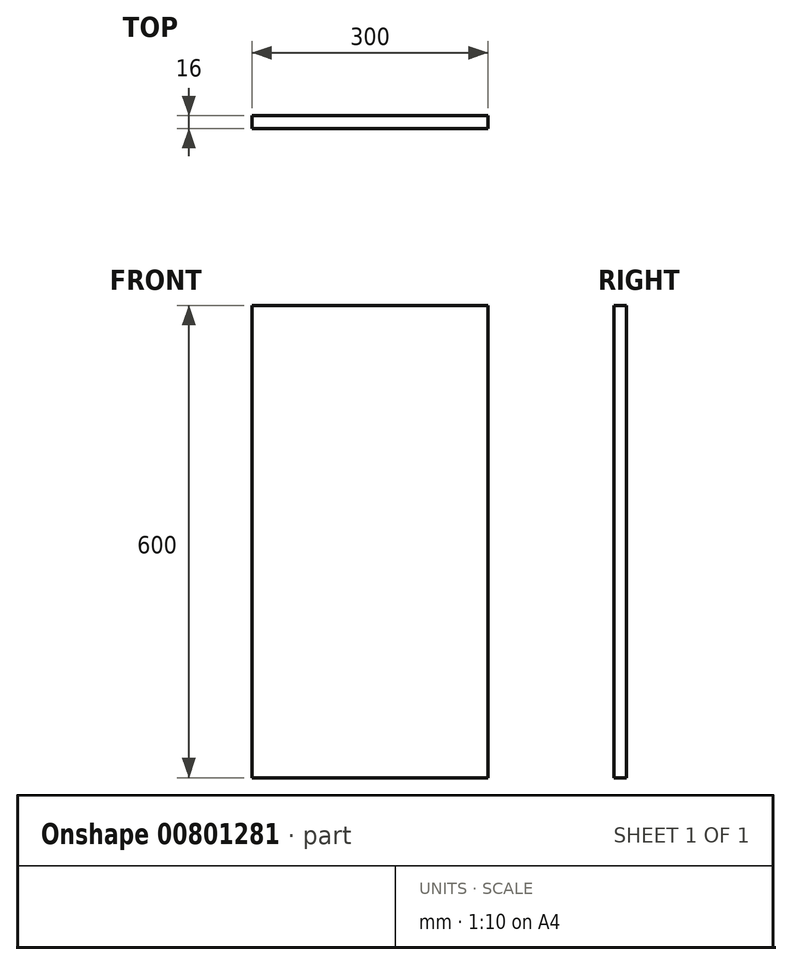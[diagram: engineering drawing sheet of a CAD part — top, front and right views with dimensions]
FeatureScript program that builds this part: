
annotation { "Feature Type Name" : "Feature", "Feature Type Description" : "" }
export const myFeature = defineFeature(function(context is Context, id is Id, definition is map)
    precondition{}
    {
        {
            var Q0;
            Q0=qCreatedBy(makeId("Front.planeOp"),FACE);
            var sketch = newSketch(context, id + "F0", { "sketchPlane" : qUnion([Q0])});
            skLineSegment(sketch, "E0.bottom", {"start": v(-150, -300) * mm, "end": v(150, -300) * mm});
            skLineSegment(sketch, "E0.top", {"start": v(-150, 300) * mm, "end": v(150, 300) * mm});
            skLineSegment(sketch, "E0.left", {"start": v(-150, -300) * mm, "end": v(-150, 300) * mm});
            skLineSegment(sketch, "E0.right", {"start": v(150, -300) * mm, "end": v(150, 300) * mm});
            skPoint(sketch, "E0.middle", {"position": v(0, 0) * mm});
            skSolve(sketch);
        }
        {
            var Q0;
            Q0=makeQuery(id+"F0.imprint","IMPRINT",FACE,{"disambiguationData":[TD([[makeQuery(id+"F0.imprint","IMPRINT",EDGE,{"derivedFrom":sQuery(id+"F0.wireOp",EDGE,"E0.bottom")}),1.0]])]});
            extrude(context, id + "F1", {"entities" : qUnion([Q0]), "depth" : 16 * mm, "offsetDistance" : 25 * mm});
        }
    });
